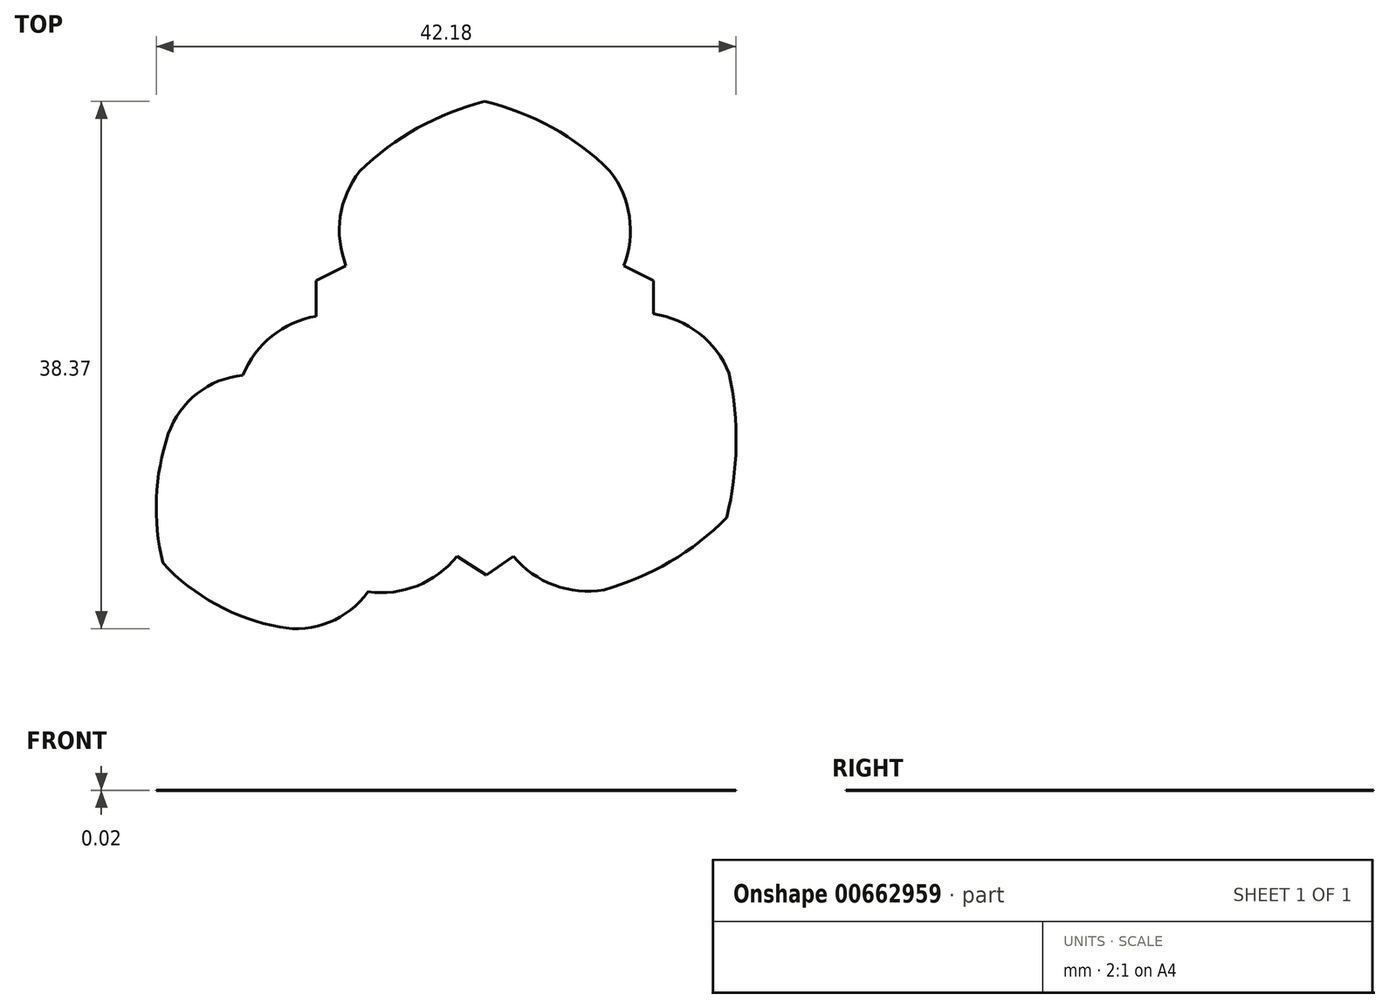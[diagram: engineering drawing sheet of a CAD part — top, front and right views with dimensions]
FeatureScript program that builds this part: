
annotation { "Feature Type Name" : "Feature", "Feature Type Description" : "" }
export const myFeature = defineFeature(function(context is Context, id is Id, definition is map)
    precondition{}
    {
        {
            var Q0;
            Q0=qCreatedBy(makeId("Top.planeOp"),FACE);
            var sketch = newSketch(context, id + "F0", { "sketchPlane" : qUnion([Q0])});
            skPoint(sketch, "E0.center", {"position": v(0, 0) * mm});
            skArc(sketch, "E1", {"start": v(-9.2, 15.13) * mm, "mid": v(-10.62, 11.82) * mm, "end": v(-10.2, 8.25) * mm});
            skLineSegment(sketch, "E2", {"start": v(-10.2, 8.25) * mm, "end": v(-12.37, 7.15) * mm});
            skLineSegment(sketch, "E3", {"start": v(-12.37, 7.15) * mm, "end": v(-12.37, 4.64) * mm});
            skLineSegment(sketch, "E4.MirrorCS", {"start": v(12.16, 7.15) * mm, "end": v(12.16, 4.64) * mm});
            skLineSegment(sketch, "E5.MirrorCS", {"start": v(10, 8.25) * mm, "end": v(12.16, 7.15) * mm});
            skArc(sketch, "E6.MirrorCS", {"start": v(9, 15.13) * mm, "mid": v(10.4, 11.82) * mm, "end": v(10, 8.25) * mm});
            skArc(sketch, "E7", {"start": v(17.66, 0.43) * mm, "mid": v(15.48, 3.32) * mm, "end": v(12.16, 4.74) * mm});
            skArc(sketch, "E8.MirrorCS", {"start": v(8.56, -15.34) * mm, "mid": v(4.94, -15) * mm, "end": v(1.97, -12.9) * mm});
            skLineSegment(sketch, "E9", {"start": v(1.97, -12.9) * mm, "end": v(0, -14.26) * mm});
            skLineSegment(sketch, "E10", {"start": v(0, -14.26) * mm, "end": v(-2.14, -12.9) * mm});
            skArc(sketch, "E11", {"start": v(-15.02, -18.05) * mm, "mid": v(-11.43, -17.7) * mm, "end": v(-8.6, -15.48) * mm});
            skArc(sketch, "E12", {"start": v(-8.6, -15.48) * mm, "mid": v(-5.03, -15.05) * mm, "end": v(-2.14, -12.9) * mm});
            skArc(sketch, "E13.MirrorCS", {"start": v(-17.7, 0.28) * mm, "mid": v(-15.6, 3.12) * mm, "end": v(-12.37, 4.57) * mm});
            skArc(sketch, "E14.MirrorCS", {"start": v(-23.14, -4) * mm, "mid": v(-21.05, -1.06) * mm, "end": v(-17.7, 0.28) * mm});
            skLineSegment(sketch, "E15", {"start": v(-12.37, 4.64) * mm, "end": v(-12.37, 4.57) * mm});
            skArc(sketch, "E16", {"start": v(-23.14, -4) * mm, "mid": v(-24, -8.66) * mm, "end": v(-23.53, -13.39) * mm});
            skArc(sketch, "E17", {"start": v(-23.53, -13.39) * mm, "mid": v(-19.66, -16.41) * mm, "end": v(-15.02, -18.05) * mm});
            skArc(sketch, "E18", {"start": v(-0.14, 20.2) * mm, "mid": v(-5, 18.26) * mm, "end": v(-9.2, 15.13) * mm});
            skArc(sketch, "E19", {"start": v(9, 15.13) * mm, "mid": v(4.78, 18.3) * mm, "end": v(-0.14, 20.2) * mm});
            skArc(sketch, "E20", {"start": v(17.49, -10.1) * mm, "mid": v(18.17, -4.84) * mm, "end": v(17.66, 0.43) * mm});
            skArc(sketch, "E21", {"start": v(8.56, -15.34) * mm, "mid": v(13.37, -13.3) * mm, "end": v(17.49, -10.1) * mm});
            skSolve(sketch);
        }
        {
            var Q0;
            Q0=makeQuery(id+"F0.imprint","IMPRINT",FACE,{"disambiguationData":[TD([[makeQuery(id+"F0.imprint","IMPRINT",EDGE,{"derivedFrom":sQuery(id+"F0.wireOp",EDGE,"E1")}),1.0]])]});
            extrude(context, id + "F1", {"entities" : qUnion([Q0]), "depth" : 7 / 406.4 * mm, "offsetDistance" : 25.4 * mm});
        }
    });
